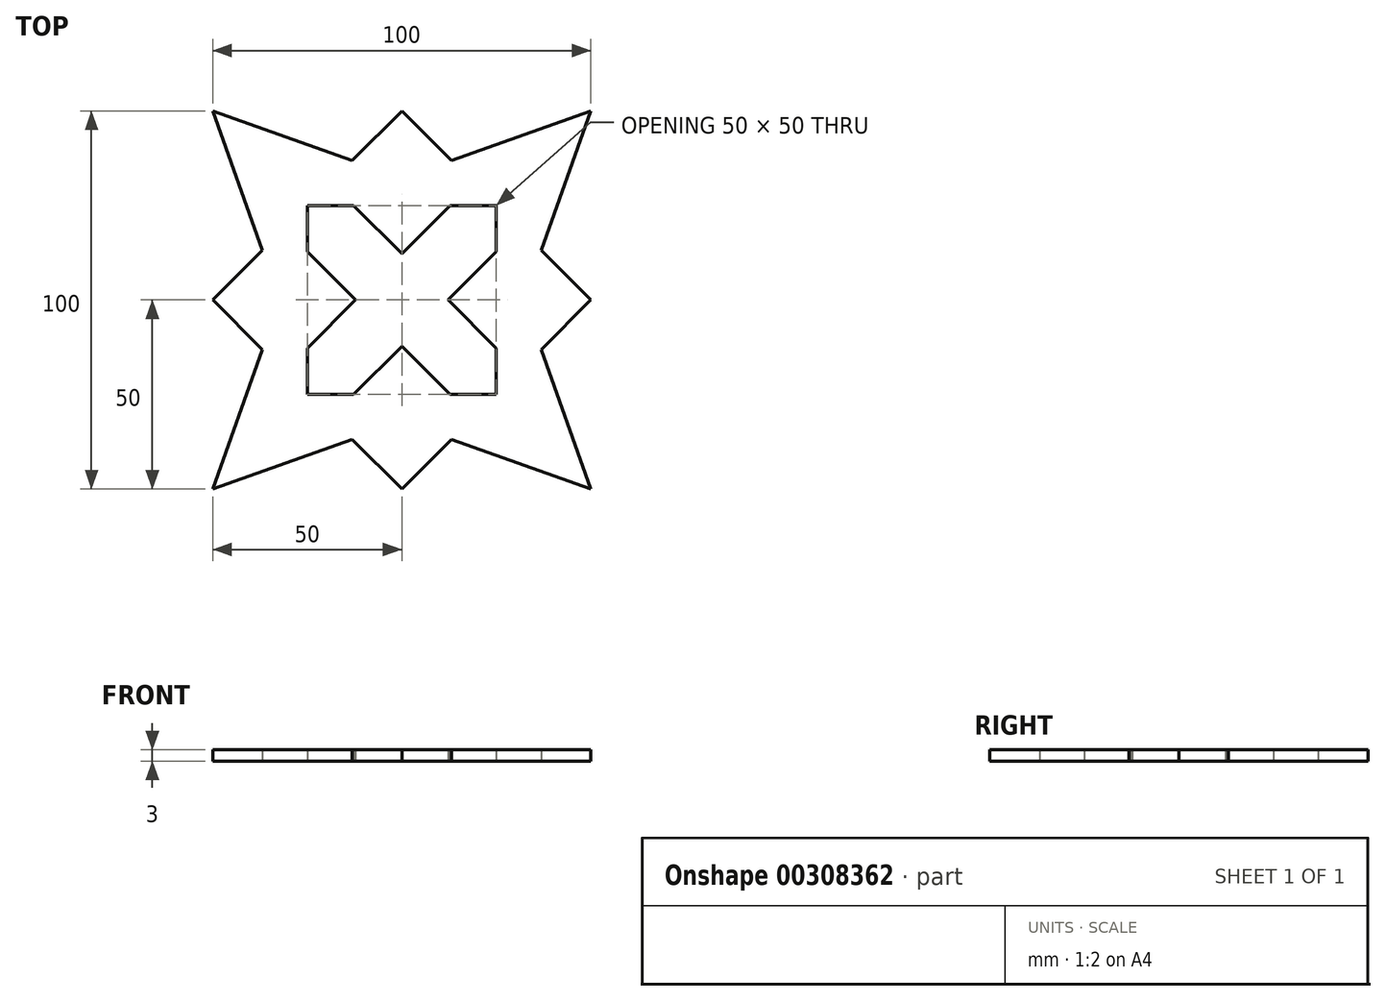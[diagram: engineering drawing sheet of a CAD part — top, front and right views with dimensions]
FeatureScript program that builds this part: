
annotation { "Feature Type Name" : "Feature", "Feature Type Description" : "" }
export const myFeature = defineFeature(function(context is Context, id is Id, definition is map)
    precondition{}
    {
        {
            var Q0;
            Q0=qCreatedBy(makeId("Top.planeOp"),FACE);
            var sketch = newSketch(context, id + "F0", { "sketchPlane" : qUnion([Q0])});
            skLineSegment(sketch, "E0.bottom", {"start": v(50, -50) * mm, "end": v(-50, -50) * mm});
            skLineSegment(sketch, "E0.top", {"start": v(50, 50) * mm, "end": v(-50, 50) * mm});
            skLineSegment(sketch, "E0.left", {"start": v(50, -50) * mm, "end": v(50, 50) * mm});
            skLineSegment(sketch, "E0.right", {"start": v(-50, -50) * mm, "end": v(-50, 50) * mm});
            skPoint(sketch, "E0.middle", {"position": v(0, 0) * mm});
            skLineSegment(sketch, "E1", {"start": v(-50, 50) * mm, "end": v(50, -50) * mm});
            skLineSegment(sketch, "E2", {"start": v(50, 50) * mm, "end": v(-50, -50) * mm});
            skLineSegment(sketch, "E3", {"start": v(0, 50) * mm, "end": v(0, -50) * mm});
            skLineSegment(sketch, "E4", {"start": v(-50, 0) * mm, "end": v(50, 0) * mm});
            skLineSegment(sketch, "E5", {"start": v(50, 0) * mm, "end": v(0, 50) * mm});
            skLineSegment(sketch, "E6", {"start": v(-50, 0) * mm, "end": v(0, 50) * mm});
            skLineSegment(sketch, "E7", {"start": v(-50, 0) * mm, "end": v(0, -50) * mm});
            skLineSegment(sketch, "E8", {"start": v(0, -50) * mm, "end": v(50, 0) * mm});
            skLineSegment(sketch, "E9", {"start": v(25, -25) * mm, "end": v(25, 25) * mm});
            skLineSegment(sketch, "E10", {"start": v(-25, 25) * mm, "end": v(25, 25) * mm});
            skLineSegment(sketch, "E11", {"start": v(-25, 25) * mm, "end": v(-25, -25) * mm});
            skLineSegment(sketch, "E12", {"start": v(-25, -25) * mm, "end": v(25, -25) * mm});
            skLineSegment(sketch, "E13", {"start": v(-50, 50) * mm, "end": v(-36.87, 13.13) * mm});
            skLineSegment(sketch, "E14", {"start": v(-36.87, 13.13) * mm, "end": v(-25, 1.27) * mm});
            skPoint(sketch, "E14.endSnap0", {"position": v(-25, 0) * mm});
            skLineSegment(sketch, "E15.MirrorCS", {"start": v(-36.87, -13.13) * mm, "end": v(-25, -1.27) * mm});
            skLineSegment(sketch, "E16.MirrorCS", {"start": v(-50, -50) * mm, "end": v(-36.87, -13.13) * mm});
            skLineSegment(sketch, "E17.MirrorCS", {"start": v(50, 50) * mm, "end": v(36.87, 13.13) * mm});
            skLineSegment(sketch, "E18.MirrorCS", {"start": v(36.87, 13.13) * mm, "end": v(25, 1.27) * mm});
            skLineSegment(sketch, "E19.MirrorCS", {"start": v(36.87, -13.13) * mm, "end": v(25, -1.27) * mm});
            skLineSegment(sketch, "E20.MirrorCS", {"start": v(50, -50) * mm, "end": v(36.87, -13.13) * mm});
            skLineSegment(sketch, "E21.MirrorCS", {"start": v(-13.13, -36.87) * mm, "end": v(-1.27, -25) * mm});
            skLineSegment(sketch, "E22.MirrorCS", {"start": v(-50, -50) * mm, "end": v(-13.13, -36.87) * mm});
            skLineSegment(sketch, "E23.MirrorCS", {"start": v(-50, 50) * mm, "end": v(-13.13, 36.87) * mm});
            skLineSegment(sketch, "E24.MirrorCS", {"start": v(-13.13, 36.87) * mm, "end": v(-1.27, 25) * mm});
            skLineSegment(sketch, "E25.MirrorCS", {"start": v(13.13, 36.87) * mm, "end": v(1.27, 25) * mm});
            skLineSegment(sketch, "E26.MirrorCS", {"start": v(50, 50) * mm, "end": v(13.13, 36.87) * mm});
            skLineSegment(sketch, "E27.MirrorCS", {"start": v(50, -50) * mm, "end": v(13.13, -36.87) * mm});
            skLineSegment(sketch, "E28.MirrorCS", {"start": v(13.13, -36.87) * mm, "end": v(1.27, -25) * mm});
            skLineSegment(sketch, "E29", {"start": v(-12.72, -25) * mm, "end": v(0, -12.28) * mm});
            skLineSegment(sketch, "E30", {"start": v(0, -12.28) * mm, "end": v(12.72, -25) * mm});
            skLineSegment(sketch, "E31.MirrorCS", {"start": v(0, 12.28) * mm, "end": v(12.72, 25) * mm});
            skLineSegment(sketch, "E32.MirrorCS", {"start": v(-12.72, 25) * mm, "end": v(0, 12.28) * mm});
            skLineSegment(sketch, "E33.MirrorCS", {"start": v(12.28, 0) * mm, "end": v(25, 12.72) * mm});
            skLineSegment(sketch, "E34.MirrorCS", {"start": v(-25, 12.72) * mm, "end": v(-12.28, 0) * mm});
            skLineSegment(sketch, "E35.MirrorCS", {"start": v(-25, -12.72) * mm, "end": v(-12.28, 0) * mm});
            skLineSegment(sketch, "E36.MirrorCS", {"start": v(12.28, 0) * mm, "end": v(25, -12.72) * mm});
            skSolve(sketch);
        }
        {
            var Q0;
            {var subQ0=sQuery(id+"F0.wireOp",EDGE,"E23.MirrorCS");Q0=makeQuery(id+"F0.imprint","IMPRINT",FACE,{"disambiguationData":[TD([[makeQuery(id+"F0.imprint","IMPRINT",EDGE,{"derivedFrom":subQ0}),-1.0]])]});}
            var Q1;
            {var subQ0=sQuery(id+"F0.wireOp",EDGE,"E13");Q1=makeQuery(id+"F0.imprint","IMPRINT",FACE,{"disambiguationData":[TD([[makeQuery(id+"F0.imprint","IMPRINT",EDGE,{"derivedFrom":subQ0}),1.0]])]});}
            var Q2;
            {var subQ3=sQuery(id+"F0.wireOp",EDGE,"E24.MirrorCS");Q2=makeQuery(id+"F0.imprint","IMPRINT",FACE,{"disambiguationData":[TD([[makeQuery(id+"F0.imprint","IMPRINT",EDGE,{"derivedFrom":subQ3}),-1.0]])]});}
            var Q3;
            {var subQ3=sQuery(id+"F0.wireOp",EDGE,"E25.MirrorCS");Q3=makeQuery(id+"F0.imprint","IMPRINT",FACE,{"disambiguationData":[TD([[makeQuery(id+"F0.imprint","IMPRINT",EDGE,{"derivedFrom":subQ3}),1.0]])]});}
            var Q4;
            {var subQ0=sQuery(id+"F0.wireOp",EDGE,"E26.MirrorCS");Q4=makeQuery(id+"F0.imprint","IMPRINT",FACE,{"disambiguationData":[TD([[makeQuery(id+"F0.imprint","IMPRINT",EDGE,{"derivedFrom":subQ0}),1.0]])]});}
            var Q5;
            {var subQ0=sQuery(id+"F0.wireOp",EDGE,"E17.MirrorCS");Q5=makeQuery(id+"F0.imprint","IMPRINT",FACE,{"disambiguationData":[TD([[makeQuery(id+"F0.imprint","IMPRINT",EDGE,{"derivedFrom":subQ0}),-1.0]])]});}
            var Q6;
            {var subQ3=sQuery(id+"F0.wireOp",EDGE,"E18.MirrorCS");Q6=makeQuery(id+"F0.imprint","IMPRINT",FACE,{"disambiguationData":[TD([[makeQuery(id+"F0.imprint","IMPRINT",EDGE,{"derivedFrom":subQ3}),-1.0]])]});}
            var Q7;
            {var subQ0=sQuery(id+"F0.wireOp",EDGE,"E33.MirrorCS");Q7=makeQuery(id+"F0.imprint","IMPRINT",FACE,{"disambiguationData":[TD([[makeQuery(id+"F0.imprint","IMPRINT",EDGE,{"derivedFrom":subQ0}),-1.0]])]});}
            var Q8;
            {var subQ0=sQuery(id+"F0.wireOp",EDGE,"E36.MirrorCS");Q8=makeQuery(id+"F0.imprint","IMPRINT",FACE,{"disambiguationData":[TD([[makeQuery(id+"F0.imprint","IMPRINT",EDGE,{"derivedFrom":subQ0}),1.0]])]});}
            var Q9;
            {var subQ3=sQuery(id+"F0.wireOp",EDGE,"E19.MirrorCS");Q9=makeQuery(id+"F0.imprint","IMPRINT",FACE,{"disambiguationData":[TD([[makeQuery(id+"F0.imprint","IMPRINT",EDGE,{"derivedFrom":subQ3}),1.0]])]});}
            var Q10;
            {var subQ0=sQuery(id+"F0.wireOp",EDGE,"E20.MirrorCS");Q10=makeQuery(id+"F0.imprint","IMPRINT",FACE,{"disambiguationData":[TD([[makeQuery(id+"F0.imprint","IMPRINT",EDGE,{"derivedFrom":subQ0}),1.0]])]});}
            var Q11;
            {var subQ0=sQuery(id+"F0.wireOp",EDGE,"E27.MirrorCS");Q11=makeQuery(id+"F0.imprint","IMPRINT",FACE,{"disambiguationData":[TD([[makeQuery(id+"F0.imprint","IMPRINT",EDGE,{"derivedFrom":subQ0}),-1.0]])]});}
            var Q12;
            {var subQ3=sQuery(id+"F0.wireOp",EDGE,"E28.MirrorCS");Q12=makeQuery(id+"F0.imprint","IMPRINT",FACE,{"disambiguationData":[TD([[makeQuery(id+"F0.imprint","IMPRINT",EDGE,{"derivedFrom":subQ3}),-1.0]])]});}
            var Q13;
            {var subQ3=sQuery(id+"F0.wireOp",EDGE,"E21.MirrorCS");Q13=makeQuery(id+"F0.imprint","IMPRINT",FACE,{"disambiguationData":[TD([[makeQuery(id+"F0.imprint","IMPRINT",EDGE,{"derivedFrom":subQ3}),1.0]])]});}
            var Q14;
            {var subQ0=sQuery(id+"F0.wireOp",EDGE,"E29");Q14=makeQuery(id+"F0.imprint","IMPRINT",FACE,{"disambiguationData":[TD([[makeQuery(id+"F0.imprint","IMPRINT",EDGE,{"derivedFrom":subQ0}),-1.0]])]});}
            var Q15;
            {var subQ0=sQuery(id+"F0.wireOp",EDGE,"E30");Q15=makeQuery(id+"F0.imprint","IMPRINT",FACE,{"disambiguationData":[TD([[makeQuery(id+"F0.imprint","IMPRINT",EDGE,{"derivedFrom":subQ0}),-1.0]])]});}
            var Q16;
            {var subQ0=sQuery(id+"F0.wireOp",EDGE,"E16.MirrorCS");Q16=makeQuery(id+"F0.imprint","IMPRINT",FACE,{"disambiguationData":[TD([[makeQuery(id+"F0.imprint","IMPRINT",EDGE,{"derivedFrom":subQ0}),-1.0]])]});}
            var Q17;
            {var subQ3=sQuery(id+"F0.wireOp",EDGE,"E15.MirrorCS");Q17=makeQuery(id+"F0.imprint","IMPRINT",FACE,{"disambiguationData":[TD([[makeQuery(id+"F0.imprint","IMPRINT",EDGE,{"derivedFrom":subQ3}),-1.0]])]});}
            var Q18;
            {var subQ0=sQuery(id+"F0.wireOp",EDGE,"E35.MirrorCS");Q18=makeQuery(id+"F0.imprint","IMPRINT",FACE,{"disambiguationData":[TD([[makeQuery(id+"F0.imprint","IMPRINT",EDGE,{"derivedFrom":subQ0}),1.0]])]});}
            var Q19;
            {var subQ0=sQuery(id+"F0.wireOp",EDGE,"E34.MirrorCS");Q19=makeQuery(id+"F0.imprint","IMPRINT",FACE,{"disambiguationData":[TD([[makeQuery(id+"F0.imprint","IMPRINT",EDGE,{"derivedFrom":subQ0}),-1.0]])]});}
            var Q20;
            {var subQ3=sQuery(id+"F0.wireOp",EDGE,"E14");Q20=makeQuery(id+"F0.imprint","IMPRINT",FACE,{"disambiguationData":[TD([[makeQuery(id+"F0.imprint","IMPRINT",EDGE,{"derivedFrom":subQ3}),1.0]])]});}
            var Q21;
            {var subQ0=sQuery(id+"F0.wireOp",EDGE,"E22.MirrorCS");Q21=makeQuery(id+"F0.imprint","IMPRINT",FACE,{"disambiguationData":[TD([[makeQuery(id+"F0.imprint","IMPRINT",EDGE,{"derivedFrom":subQ0}),1.0]])]});}
            var Q22;
            {var subQ5=sQuery(id+"F0.wireOp",EDGE,"E15.MirrorCS");Q22=makeQuery(id+"F0.imprint","IMPRINT",FACE,{"disambiguationData":[TD([[makeQuery(id+"F0.imprint","IMPRINT",EDGE,{"derivedFrom":subQ5}),1.0]])]});}
            var Q23;
            {var subQ5=sQuery(id+"F0.wireOp",EDGE,"E14");Q23=makeQuery(id+"F0.imprint","IMPRINT",FACE,{"disambiguationData":[TD([[makeQuery(id+"F0.imprint","IMPRINT",EDGE,{"derivedFrom":subQ5}),-1.0]])]});}
            var Q24;
            {var subQ5=sQuery(id+"F0.wireOp",EDGE,"E24.MirrorCS");Q24=makeQuery(id+"F0.imprint","IMPRINT",FACE,{"disambiguationData":[TD([[makeQuery(id+"F0.imprint","IMPRINT",EDGE,{"derivedFrom":subQ5}),1.0]])]});}
            var Q25;
            {var subQ5=sQuery(id+"F0.wireOp",EDGE,"E25.MirrorCS");Q25=makeQuery(id+"F0.imprint","IMPRINT",FACE,{"disambiguationData":[TD([[makeQuery(id+"F0.imprint","IMPRINT",EDGE,{"derivedFrom":subQ5}),-1.0]])]});}
            var Q26;
            {var subQ5=sQuery(id+"F0.wireOp",EDGE,"E18.MirrorCS");Q26=makeQuery(id+"F0.imprint","IMPRINT",FACE,{"disambiguationData":[TD([[makeQuery(id+"F0.imprint","IMPRINT",EDGE,{"derivedFrom":subQ5}),1.0]])]});}
            var Q27;
            {var subQ5=sQuery(id+"F0.wireOp",EDGE,"E19.MirrorCS");Q27=makeQuery(id+"F0.imprint","IMPRINT",FACE,{"disambiguationData":[TD([[makeQuery(id+"F0.imprint","IMPRINT",EDGE,{"derivedFrom":subQ5}),-1.0]])]});}
            var Q28;
            {var subQ5=sQuery(id+"F0.wireOp",EDGE,"E28.MirrorCS");Q28=makeQuery(id+"F0.imprint","IMPRINT",FACE,{"disambiguationData":[TD([[makeQuery(id+"F0.imprint","IMPRINT",EDGE,{"derivedFrom":subQ5}),1.0]])]});}
            var Q29;
            {var subQ5=sQuery(id+"F0.wireOp",EDGE,"E21.MirrorCS");Q29=makeQuery(id+"F0.imprint","IMPRINT",FACE,{"disambiguationData":[TD([[makeQuery(id+"F0.imprint","IMPRINT",EDGE,{"derivedFrom":subQ5}),-1.0]])]});}
            var Q30;
            {var subQ0=sQuery(id+"F0.wireOp",EDGE,"E32.MirrorCS");Q30=makeQuery(id+"F0.imprint","IMPRINT",FACE,{"disambiguationData":[TD([[makeQuery(id+"F0.imprint","IMPRINT",EDGE,{"derivedFrom":subQ0}),1.0]])]});}
            var Q31;
            {var subQ0=sQuery(id+"F0.wireOp",EDGE,"E31.MirrorCS");Q31=makeQuery(id+"F0.imprint","IMPRINT",FACE,{"disambiguationData":[TD([[makeQuery(id+"F0.imprint","IMPRINT",EDGE,{"derivedFrom":subQ0}),1.0]])]});}
            extrude(context, id + "F1", {"entities" : qUnion([Q0, Q1, Q2, Q3, Q4, Q5, Q6, Q7, Q8, Q9, Q10, Q11, Q12, Q13, Q14, Q15, Q16, Q17, Q18, Q19, Q20, Q21, Q22, Q23, Q24, Q25, Q26, Q27, Q28, Q29, Q30, Q31]), "depth" : 3 * mm});
        }
    });
